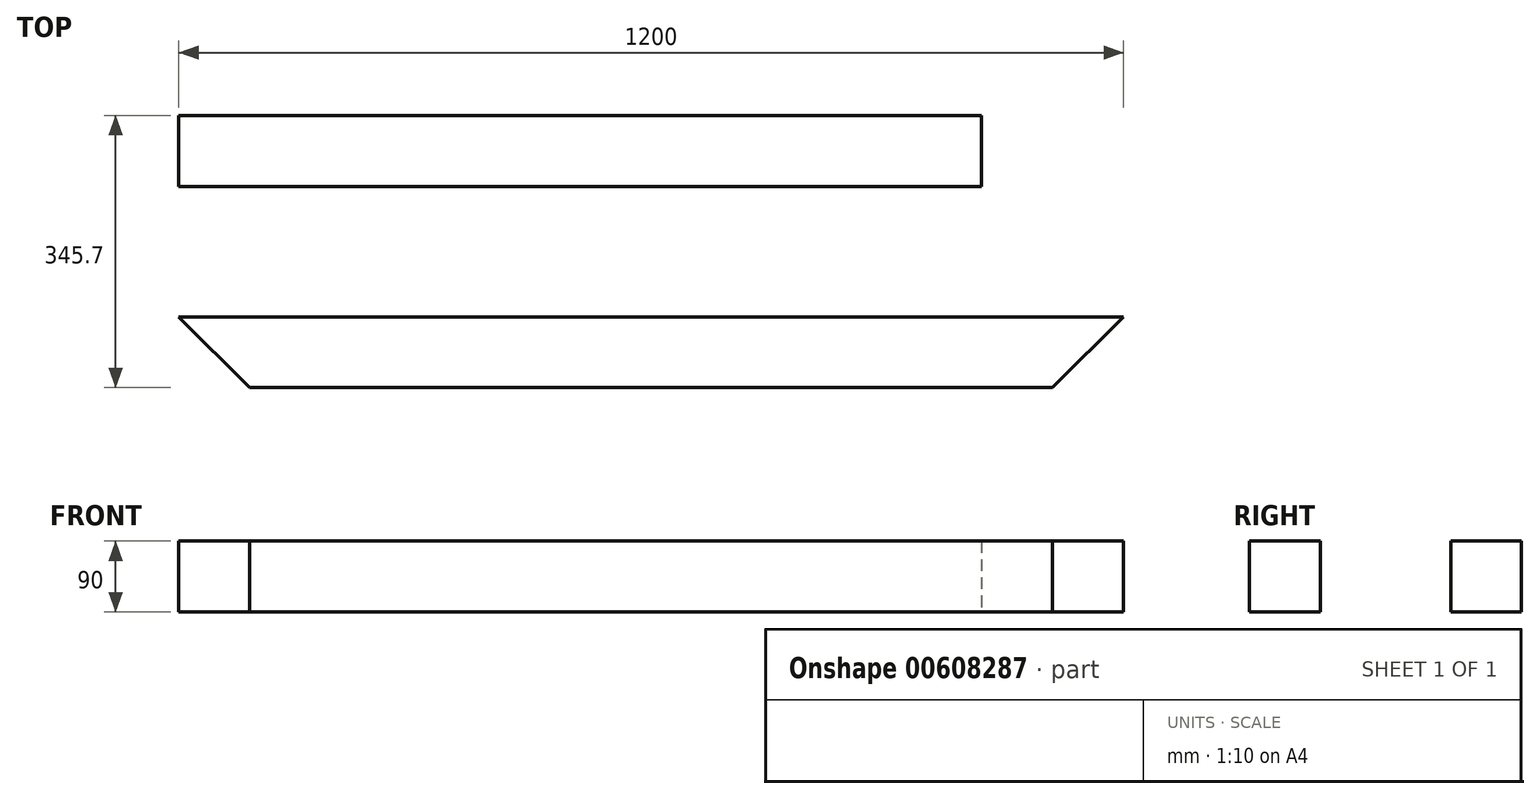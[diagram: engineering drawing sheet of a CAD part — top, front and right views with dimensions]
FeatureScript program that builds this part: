
annotation { "Feature Type Name" : "Feature", "Feature Type Description" : "" }
export const myFeature = defineFeature(function(context is Context, id is Id, definition is map)
    precondition{}
    {
        {
            var Q0;
            Q0=qCreatedBy(makeId("Top.planeOp"),FACE);
            var sketch = newSketch(context, id + "F0", { "sketchPlane" : qUnion([Q0])});
            skLineSegment(sketch, "E0.bottom", {"start": v(0, 0) * mm, "end": v(1200, 0) * mm});
            skLineSegment(sketch, "E0.top", {"start": v(0, -90) * mm, "end": v(1200, -90) * mm});
            skLineSegment(sketch, "E0.left", {"start": v(0, 0) * mm, "end": v(0, -90) * mm});
            skLineSegment(sketch, "E0.right", {"start": v(1200, 0) * mm, "end": v(1200, -90) * mm});
            skSolve(sketch);
        }
        {
            var Q0;
            Q0=makeQuery(id+"F0.imprint","IMPRINT",FACE,{"disambiguationData":[TD([[makeQuery(id+"F0.imprint","IMPRINT",EDGE,{"derivedFrom":sQuery(id+"F0.wireOp",EDGE,"E0.bottom")}),-1.0]])]});
            extrude(context, id + "F1", {"entities" : qUnion([Q0]), "depth" : 90 * mm, "offsetDistance" : 25 * mm});
        }
        {
            var Q0;
            Q0=makeQuery(id+"F1.opExtrude","SWEPT_EDGE",EDGE,{"disambiguationData":[OSD([sQuery(id+"F0.wireOp",EDGE,"E0.top"),sQuery(id+"F0.wireOp",EDGE,"E0.right")])]});
            var Q1;
            Q1=makeQuery(id+"F1.opExtrude","SWEPT_EDGE",EDGE,{"disambiguationData":[OSD([sQuery(id+"F0.wireOp",EDGE,"E0.top"),sQuery(id+"F0.wireOp",EDGE,"E0.left")])]});
            chamfer(context, id + "F2", {"entities" : qUnion([Q0, Q1]), "width" : 90 * mm, "tangentPropagation" : true});
        }
        {
            var Q0;
            Q0=qCreatedBy(makeId("Top.planeOp"),FACE);
            var sketch = newSketch(context, id + "F3", { "sketchPlane" : qUnion([Q0])});
            skLineSegment(sketch, "E1.bottom", {"start": v(0, 255.7) * mm, "end": v(1020, 255.7) * mm});
            skLineSegment(sketch, "E1.top", {"start": v(0, 165.7) * mm, "end": v(1020, 165.7) * mm});
            skLineSegment(sketch, "E1.left", {"start": v(0, 255.7) * mm, "end": v(0, 165.7) * mm});
            skLineSegment(sketch, "E1.right", {"start": v(1020, 255.7) * mm, "end": v(1020, 165.7) * mm});
            skSolve(sketch);
        }
        {
            var Q0;
            Q0=makeQuery(id+"F3.imprint","IMPRINT",FACE,{"disambiguationData":[TD([[makeQuery(id+"F3.imprint","IMPRINT",EDGE,{"derivedFrom":sQuery(id+"F3.wireOp",EDGE,"E1.bottom")}),-1.0]])]});
            extrude(context, id + "F4", {"entities" : qUnion([Q0]), "depth" : 90 * mm, "offsetDistance" : 25 * mm});
        }
    });
